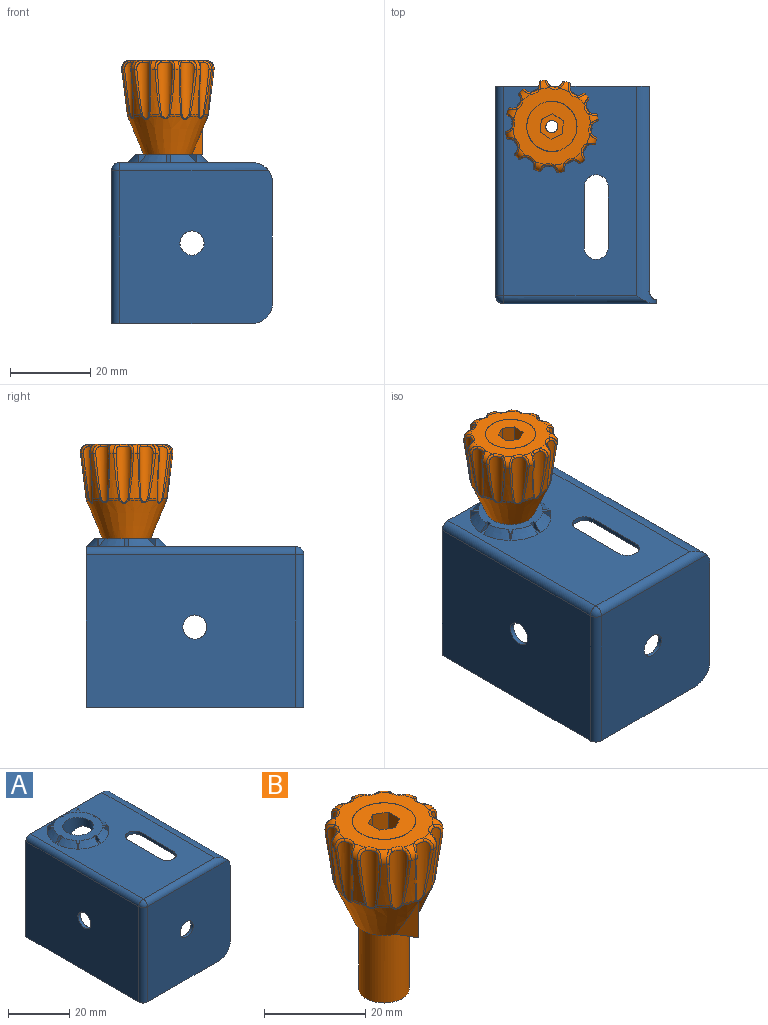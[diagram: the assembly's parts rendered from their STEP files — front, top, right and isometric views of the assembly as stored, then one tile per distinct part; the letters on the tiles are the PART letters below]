
ASSEMBLY  parts=2 mates=1
PART A: 58 faces, bbox 40.1x54.1x42.1 mm
  f0: plane 52x33mm, normal (0,0,1), area 1293.7mm2, adj f5,f6,f12,f13,f14,f15,f17,f18
  f1: plane 51x19.73mm, normal (0,0,-1), area 886.5mm2, adj f5,f6,f9,f12,f13,f14,f15,f16
  f2: plane 54x35mm, normal (0,0,-1), area 96.3mm2, adj f4,f6,f7,f8,f10,f11,f31,f33
  f3: plane 30x1mm, normal (1,0,0), area 30mm2, adj f4,f5,f8,f11
  f4: cylinder r=5mm len=5mm, axis (0,-1,0), area 7.9mm2, adj f2,f3,f8,f11
  f5: cylinder r=5mm len=54mm, axis (0,-1,0), area 189.4mm2, adj f0,f1,f3,f6,f8,f11,f30,f32
  f6: plane 40x38.2mm, normal (0,1,0), area 236.8mm2, adj f0,f1,f2,f5,f7,f9,f10,f35
  f7: plane 52x38mm, normal (-1,0,0), area 1947.7mm2, adj f2,f6,f33,f35,f36
  f8: plane 38x38mm, normal (0,-1,0), area 1409.4mm2, adj f2,f3,f4,f5,f32,f33,f37
  f9: plane 53x17.31mm, normal (0.71,0,-0.71), area 1178.5mm2, adj f1,f6,f10,f11,f16,f30,f31,f36
  f10: plane 51x21.54mm, normal (1,0,0), area 1075.4mm2, adj f2,f6,f9,f31,f36
  f11: plane 36.84x36.84mm, normal (0,1,0), area 1235.1mm2, adj f2,f3,f4,f5,f9,f30,f31,f37
  f12: plane 15x1.16mm, normal (-1,0,0), area 17.3mm2, adj f0,f1,f13,f15
  f13: cylinder r=3mm len=6mm, axis (0,0,1), area 10.9mm2, adj f0,f1,f12,f14
  f14: plane 15x1.16mm, normal (1,0,0), area 17.3mm2, adj f0,f1,f13,f15
  f15: cylinder r=3mm len=6mm, axis (0,0,1), area 10.9mm2, adj f0,f1,f12,f14
  f16: cylinder r=5mm len=12.67mm, axis (0,0,1), area 241.1mm2, adj f1,f9,f29
  f17: plane 2.55x2.01mm, normal (0,-1,0), area 3.1mm2, adj f0,f18,f29,f42
  f18: plane 2x1mm, normal (-1,0,0), area 2mm2, adj f0,f17,f19,f29
  f19: plane 2.55x2.01mm, normal (0,1,0), area 3.1mm2, adj f0,f18,f29,f41
  f20: plane 2.55x2.01mm, normal (1,0,0), area 3.1mm2, adj f0,f21,f29,f40
  f21: plane 2x1mm, normal (0,-1,0), area 2mm2, adj f0,f20,f22,f29
  f22: plane 2.55x2.01mm, normal (-1,0,0), area 3.1mm2, adj f0,f21,f29,f44
  f23: plane 2.55x2.01mm, normal (0,1,0), area 3.1mm2, adj f0,f24,f29,f39
  f24: plane 2x1mm, normal (1,0,0), area 2mm2, adj f0,f23,f25,f29
  f25: plane 2.55x2.01mm, normal (0,-1,0), area 3.1mm2, adj f0,f24,f29,f38
  f26: plane 2.55x2.01mm, normal (-1,0,0), area 3.1mm2, adj f0,f27,f29,f45
  f27: plane 2x1mm, normal (0,1,0), area 2mm2, adj f0,f26,f28,f29
  f28: plane 2.55x2.01mm, normal (1,0,0), area 3.1mm2, adj f0,f27,f29,f43
  f29: plane 15.97x15.97mm, normal (0,0,1), area 125.2mm2, adj f16,f17,f18,f19,f20,f21,f22,f23
  f30: cylinder r=2mm len=23.18mm, axis (1,0,0), area 66.3mm2, adj f1,f5,f9,f11
  f31: cylinder r=2mm len=23.54mm, axis (0,0,1), area 69.9mm2, adj f2,f9,f10,f11
  f32: cylinder r=2mm len=37mm, axis (-1,0,0), area 110.7mm2, adj f0,f5,f8,f34
  f33: cylinder r=2mm len=38mm, axis (0,0,-1), area 119.4mm2, adj f2,f7,f8,f34
  f34: sphere r=2mm, area 6.3mm2, adj f32,f33,f35
  f35: cylinder r=2mm len=52mm, axis (0,-1,0), area 163.4mm2, adj f0,f6,f7,f34
  f36: cylinder r=3mm len=6mm, axis (-1,0,0), area 27.7mm2, adj f7,f9,f10
  f37: cylinder r=3mm len=6mm, axis (0,-1,0), area 18.8mm2, adj f8,f11
  f38: cone r=10mm half-angle=45deg, axis (0,0,-1), area 17.5mm2, adj f0,f25,f29,f46
  f39: cone r=8mm half-angle=45deg, axis (0,0,-1), area 17.8mm2, adj f0,f23,f29,f49
  f40: cone r=10mm half-angle=45deg, axis (0,0,-1), area 17.8mm2, adj f0,f20,f29,f55
  f41: cone r=8mm half-angle=45deg, axis (0,0,-1), area 17.8mm2, adj f0,f19,f29,f56
  f42: cone r=8mm half-angle=45deg, axis (0,0,-1), area 17.5mm2, adj f0,f17,f29,f52
  f43: cone r=8mm half-angle=45deg, axis (0,0,-1), area 17.8mm2, adj f0,f28,f29,f53
  f44: cone r=8mm half-angle=45deg, axis (0,0,-1), area 17.5mm2, adj f0,f22,f29,f50
  f45: cone r=8mm half-angle=45deg, axis (0,0,-1), area 17.5mm2, adj f0,f26,f29,f48
  f46: plane 2.06x1.82mm, normal (0.85,-0.53,0), area 2.1mm2, adj f29,f38,f47
  f47: cylinder r=10mm len=2mm, axis (0,0,-1), area 0.3mm2, adj f0,f29,f46,f48
  f48: plane 2.06x1.82mm, normal (-0.53,0.85,0), area 2.1mm2, adj f29,f45,f47
  f49: plane 2.06x1.82mm, normal (0.85,0.53,0), area 2.1mm2, adj f29,f39,f51
  f50: plane 2.06x1.82mm, normal (-0.53,-0.85,0), area 2.1mm2, adj f29,f44,f51
  f51: cylinder r=10mm len=2mm, axis (0,0,-1), area 0.3mm2, adj f0,f29,f49,f50
  f52: plane 2.06x1.82mm, normal (-0.85,-0.53,0), area 2.1mm2, adj f29,f42,f54
  f53: plane 2.06x1.82mm, normal (0.53,0.85,0), area 2.1mm2, adj f29,f43,f54
  f54: cylinder r=10mm len=2mm, axis (0,0,-1), area 0.3mm2, adj f0,f29,f52,f53
  f55: plane 2.06x2mm, normal (0.53,-0.85,0), area 2.5mm2, adj f0,f29,f40,f57
  f56: plane 2.06x2mm, normal (-0.85,0.53,0), area 2.5mm2, adj f0,f29,f41,f57
  f57: cylinder r=0.02mm len=2mm, axis (0,0,-1), area 0.1mm2, adj f0,f29,f55,f56
PART B: 171 faces, bbox 23.8x23.8x41.5 mm
  f0: cylinder r=1.5mm len=5.5mm, axis (0,0,1), area 51.8mm2, adj f40,f159
  f1: plane 12.45x12.45mm, normal (0,0,1), area 95.5mm2, adj f152,f153,f154,f155,f156,f157,f158
  f2: torus R=9.64mm, axis (0,0,-1), area 4.8mm2, adj f14,f43,f56,f91
  f3: torus R=9.64mm, axis (0,0,-1), area 4.8mm2, adj f16,f43,f138,f145
  f4: torus R=9.64mm, axis (0,0,-1), area 4.8mm2, adj f17,f43,f64,f99
  f5: torus R=9.64mm, axis (0,0,-1), area 4.8mm2, adj f19,f43,f59,f72
  f6: torus R=9.64mm, axis (0,0,-1), area 4.8mm2, adj f21,f43,f67,f83
  f7: torus R=9.64mm, axis (0,0,-1), area 4.8mm2, adj f22,f43,f108,f146
  f8: torus R=9.64mm, axis (0,0,-1), area 4.8mm2, adj f15,f43,f88,f137
  f9: torus R=9.64mm, axis (0,0,-1), area 4.8mm2, adj f23,f43,f96,f124
  f10: torus R=9.64mm, axis (0,0,-1), area 4.8mm2, adj f24,f43,f104,f131
  f11: torus R=9.64mm, axis (0,0,-1), area 4.8mm2, adj f20,f43,f80,f112
  f12: torus R=9.64mm, axis (0,0,-1), area 4.8mm2, adj f18,f43,f76,f120
  f13: torus R=9.64mm, axis (0,0,-1), area 4.8mm2, adj f25,f43,f115,f128
  f14: cone r=10.11mm half-angle=7.8deg, axis (0,0,1), area 18.4mm2, adj f2,f30,f58,f93
  f15: cone r=10.11mm half-angle=7.8deg, axis (0,0,1), area 18.4mm2, adj f8,f28,f90,f139
  f16: cone r=10.11mm half-angle=7.8deg, axis (0,0,1), area 18.4mm2, adj f3,f27,f140,f147
  f17: cone r=10.11mm half-angle=7.8deg, axis (0,0,1), area 18.4mm2, adj f4,f32,f66,f101
  f18: cone r=10.11mm half-angle=7.8deg, axis (0,0,1), area 18.4mm2, adj f12,f31,f78,f121
  f19: cone r=10.11mm half-angle=7.8deg, axis (0,0,1), area 18.4mm2, adj f5,f26,f61,f73
  f20: cone r=10.11mm half-angle=7.8deg, axis (0,0,1), area 18.4mm2, adj f11,f33,f82,f114
  f21: cone r=10.11mm half-angle=7.8deg, axis (0,0,1), area 18.4mm2, adj f6,f29,f69,f85
  f22: cone r=10.11mm half-angle=7.8deg, axis (0,0,1), area 18.4mm2, adj f7,f34,f110,f148
  f23: cone r=10.11mm half-angle=7.8deg, axis (0,0,1), area 18.4mm2, adj f9,f37,f98,f126
  f24: cone r=10.11mm half-angle=7.8deg, axis (0,0,1), area 18.4mm2, adj f10,f35,f105,f133
  f25: cone r=10.11mm half-angle=7.8deg, axis (0,0,1), area 18.4mm2, adj f13,f36,f117,f130
  f26: torus R=8.13mm, axis (0,0,-1), area 1.5mm2, adj f19,f38,f63,f75
  f27: torus R=8.13mm, axis (0,0,-1), area 1.5mm2, adj f16,f38,f142,f149
  f28: torus R=8.13mm, axis (0,0,-1), area 1.5mm2, adj f15,f38,f92,f141
  f29: torus R=8.13mm, axis (0,0,-1), area 1.5mm2, adj f21,f38,f71,f87
  f30: torus R=8.13mm, axis (0,0,-1), area 1.5mm2, adj f14,f38,f60,f95
  f31: torus R=8.13mm, axis (0,0,-1), area 1.5mm2, adj f18,f38,f79,f123
  f32: torus R=8.13mm, axis (0,0,-1), area 1.5mm2, adj f17,f38,f68,f103
  f33: torus R=8.13mm, axis (0,0,-1), area 1.5mm2, adj f20,f38,f84,f116
  f34: torus R=8.13mm, axis (0,0,-1), area 1.5mm2, adj f22,f38,f111,f150
  f35: torus R=8.13mm, axis (0,0,-1), area 1.5mm2, adj f24,f38,f107,f135
  f36: torus R=8.13mm, axis (0,0,-1), area 1.5mm2, adj f25,f38,f119,f132
  f37: torus R=8.13mm, axis (0,0,-1), area 1.5mm2, adj f23,f38,f100,f127
  f38: cone r=6mm half-angle=22.6deg, axis (0,0,1), area 482.2mm2, adj f26,f27,f28,f29,f30,f31,f32,f33
  f39: cylinder r=5mm len=17mm, axis (0,0,1), area 534.1mm2, adj f40,f41
  f40: plane 10x10mm, normal (0,0,-1), area 71.5mm2, adj f0,f39
  f41: plane 15.64x12mm, normal (0,0,-1), area 42.8mm2, adj f38,f39,f169,f170
  f42: torus R=6.25mm, axis (0,0,-1), area 1.2mm2, adj f43,f152
  f43: plane 19.12x19.1mm, normal (0,0,1), area 160.1mm2, adj f2,f3,f4,f5,f6,f7,f8,f9
  f44: cylinder r=2mm len=13.83mm, axis (0,0,1), area 47.1mm2, adj f128,f129,f130,f131,f132,f133,f134,f135
  f45: cylinder r=2mm len=13.94mm, axis (0,0,1), area 48.6mm2, adj f120,f121,f122,f123,f124,f125,f126,f127
  f46: cylinder r=2mm len=13.94mm, axis (0,0,1), area 48.6mm2, adj f112,f113,f114,f115,f116,f117,f118,f119
  f47: cylinder r=2mm len=13.94mm, axis (0,0,1), area 48.6mm2, adj f104,f105,f106,f107,f108,f109,f110,f111
  f48: cylinder r=2mm len=13.83mm, axis (0,0,1), area 47.1mm2, adj f96,f97,f98,f99,f100,f101,f102,f103
  f49: cylinder r=2mm len=13.83mm, axis (0,0,1), area 47.1mm2, adj f88,f89,f90,f91,f92,f93,f94,f95
  f50: cylinder r=2mm len=13.83mm, axis (0,0,1), area 47.1mm2, adj f144,f145,f146,f147,f148,f149,f150,f151
  f51: cylinder r=2mm len=13.83mm, axis (0,0,1), area 47.1mm2, adj f80,f81,f82,f83,f84,f85,f86,f87
  f52: cylinder r=2mm len=13.83mm, axis (0,0,1), area 47.1mm2, adj f72,f73,f74,f75,f76,f77,f78,f79
  f53: cylinder r=2mm len=13.94mm, axis (0,0,1), area 48.6mm2, adj f64,f65,f66,f67,f68,f69,f70,f71
  f54: cylinder r=2mm len=13.94mm, axis (0,0,1), area 48.6mm2, adj f136,f137,f138,f139,f140,f141,f142,f143
  f55: cylinder r=2mm len=13.94mm, axis (0,0,1), area 48.6mm2, adj f56,f57,f58,f59,f60,f61,f62,f63
  f56: bspline ~2.74x2.27mm, area 2.2mm2, adj f2,f55,f57,f58
  f57: torus R=2.5mm, axis (0,0,1), area 1.9mm2, adj f43,f55,f56,f59
  f58: bspline ~15.1x2.39mm, area 6.2mm2, adj f14,f55,f56,f60
  f59: bspline ~2.64x2.44mm, area 2.2mm2, adj f5,f55,f57,f61
  f60: bspline ~0.87x0.6mm, area 0.2mm2, adj f30,f55,f58,f62
  f61: bspline ~12.62x2.15mm, area 6.2mm2, adj f19,f55,f59,f63
  f62: bspline ~2.6x1.52mm, area 0.7mm2, adj f38,f55,f60,f63
  f63: bspline ~0.85x0.38mm, area 0.2mm2, adj f26,f55,f61,f62
  f64: bspline ~2.74x2.12mm, area 2.2mm2, adj f4,f53,f65,f66
  f65: torus R=2.5mm, axis (0,0,1), area 1.9mm2, adj f43,f53,f64,f67
  f66: bspline ~15.1x2mm, area 6.2mm2, adj f17,f53,f64,f68
  f67: bspline ~2.44x2.22mm, area 2.2mm2, adj f6,f53,f65,f69
  f68: bspline ~0.87x0.59mm, area 0.2mm2, adj f32,f53,f66,f70
  f69: bspline ~12.62x1.66mm, area 6.2mm2, adj f21,f53,f67,f71
  f70: bspline ~3x1.52mm, area 0.7mm2, adj f38,f53,f68,f71
  f71: bspline ~0.85x0.49mm, area 0.2mm2, adj f29,f53,f69,f70
  f72: bspline ~2.74x2.09mm, area 2.2mm2, adj f5,f52,f73,f74
  f73: bspline ~14.64x1.94mm, area 6mm2, adj f19,f52,f72,f75
  f74: torus R=2.5mm, axis (0,0,1), area 1.8mm2, adj f43,f52,f72,f76
  f75: bspline ~0.86x0.58mm, area 0.2mm2, adj f26,f52,f73,f77
  f76: bspline ~2.75x2.2mm, area 2.2mm2, adj f12,f52,f74,f78
  f77: bspline ~2.82x1.35mm, area 0.6mm2, adj f38,f52,f75,f79
  f78: bspline ~15.26x2mm, area 6mm2, adj f18,f52,f76,f79
  f79: bspline ~0.84x0.49mm, area 0.2mm2, adj f31,f52,f77,f78
  f80: bspline ~2.75x2.51mm, area 2.2mm2, adj f11,f51,f81,f82
  f81: torus R=2.5mm, axis (0,0,1), area 1.8mm2, adj f43,f51,f80,f83
  f82: bspline ~15.26x2.46mm, area 6mm2, adj f20,f51,f80,f84
  f83: bspline ~2.74x2.47mm, area 2.2mm2, adj f6,f51,f81,f85
  f84: bspline ~0.84x0.5mm, area 0.2mm2, adj f33,f51,f82,f86
  f85: bspline ~14.64x2.41mm, area 6mm2, adj f21,f51,f83,f87
  f86: bspline ~2.44x1.41mm, area 0.6mm2, adj f38,f51,f84,f87
  f87: bspline ~0.86x0.45mm, area 0.2mm2, adj f29,f51,f85,f86
  f88: bspline ~2.74x2.47mm, area 2.2mm2, adj f8,f49,f89,f90
  f89: torus R=2.5mm, axis (0,0,1), area 1.8mm2, adj f43,f49,f88,f91
  f90: bspline ~14.64x2.41mm, area 6mm2, adj f15,f49,f88,f92
  f91: bspline ~2.75x2.51mm, area 2.2mm2, adj f2,f49,f89,f93
  f92: bspline ~0.86x0.45mm, area 0.2mm2, adj f28,f49,f90,f94
  f93: bspline ~15.26x2.46mm, area 6mm2, adj f14,f49,f91,f95
  f94: bspline ~2.44x1.41mm, area 0.6mm2, adj f38,f49,f92,f95
  f95: bspline ~0.84x0.5mm, area 0.2mm2, adj f30,f49,f93,f94
  f96: bspline ~2.74x2.28mm, area 2.2mm2, adj f9,f48,f97,f98
  f97: torus R=2.5mm, axis (0,0,1), area 1.8mm2, adj f43,f48,f96,f99
  f98: bspline ~14.64x2.34mm, area 6mm2, adj f23,f48,f96,f100
  f99: bspline ~2.75x2.67mm, area 2.2mm2, adj f4,f48,f97,f101
  f100: bspline ~0.86x0.6mm, area 0.2mm2, adj f37,f48,f98,f102
  f101: bspline ~15.26x2.51mm, area 6mm2, adj f17,f48,f99,f103
  f102: bspline ~2.44x1.41mm, area 0.6mm2, adj f38,f48,f100,f103
  f103: bspline ~0.84x0.37mm, area 0.2mm2, adj f32,f48,f101,f102
  f104: bspline ~2.74x2.48mm, area 2.2mm2, adj f10,f47,f105,f106
  f105: bspline ~15.1x2.47mm, area 6.2mm2, adj f24,f47,f104,f107
  f106: torus R=2.5mm, axis (0,0,1), area 1.9mm2, adj f43,f47,f104,f108
  f107: bspline ~0.87x0.46mm, area 0.2mm2, adj f35,f47,f105,f109
  f108: bspline ~2.46x2.44mm, area 2.2mm2, adj f7,f47,f106,f110
  f109: bspline ~2.6x1.52mm, area 0.7mm2, adj f38,f47,f107,f111
  f110: bspline ~12.62x2.16mm, area 6.2mm2, adj f22,f47,f108,f111
  f111: bspline ~0.85x0.51mm, area 0.2mm2, adj f34,f47,f109,f110
  f112: bspline ~2.74x2.27mm, area 2.2mm2, adj f11,f46,f113,f114
  f113: torus R=2.5mm, axis (0,0,1), area 1.9mm2, adj f43,f46,f112,f115
  f114: bspline ~15.1x2.39mm, area 6.2mm2, adj f20,f46,f112,f116
  f115: bspline ~2.64x2.44mm, area 2.2mm2, adj f13,f46,f113,f117
  f116: bspline ~0.87x0.6mm, area 0.2mm2, adj f33,f46,f114,f118
  f117: bspline ~12.62x2.15mm, area 6.2mm2, adj f25,f46,f115,f119
  f118: bspline ~2.32x1.52mm, area 0.7mm2, adj f38,f46,f116,f119
  f119: bspline ~0.85x0.38mm, area 0.2mm2, adj f36,f46,f117,f118
  f120: bspline ~2.74x2.48mm, area 2.2mm2, adj f12,f45,f121,f122
  f121: bspline ~15.1x2.47mm, area 6.2mm2, adj f18,f45,f120,f123
  f122: torus R=2.5mm, axis (0,0,1), area 1.9mm2, adj f43,f45,f120,f124
  f123: bspline ~0.87x0.46mm, area 0.2mm2, adj f31,f45,f121,f125
  f124: bspline ~2.46x2.44mm, area 2.2mm2, adj f9,f45,f122,f126
  f125: bspline ~2.6x1.52mm, area 0.7mm2, adj f38,f45,f123,f127
  f126: bspline ~12.62x2.16mm, area 6.2mm2, adj f23,f45,f124,f127
  f127: bspline ~0.85x0.51mm, area 0.2mm2, adj f37,f45,f125,f126
  f128: bspline ~2.74x2.09mm, area 2.2mm2, adj f13,f44,f129,f130
  f129: torus R=2.5mm, axis (0,0,1), area 1.8mm2, adj f43,f44,f128,f131
  f130: bspline ~14.64x1.94mm, area 6mm2, adj f25,f44,f128,f132
  f131: bspline ~2.75x2.2mm, area 2.2mm2, adj f10,f44,f129,f133
  f132: bspline ~0.86x0.58mm, area 0.2mm2, adj f36,f44,f130,f134
  f133: bspline ~15.26x2mm, area 6mm2, adj f24,f44,f131,f135
  f134: bspline ~2.82x1.35mm, area 0.6mm2, adj f38,f44,f132,f135
  f135: bspline ~0.84x0.49mm, area 0.2mm2, adj f35,f44,f133,f134
  f136: torus R=2.5mm, axis (0,0,1), area 1.9mm2, adj f43,f54,f137,f138
  f137: bspline ~2.44x2.22mm, area 2.2mm2, adj f8,f54,f136,f139
  f138: bspline ~2.74x2.12mm, area 2.2mm2, adj f3,f54,f136,f140
  f139: bspline ~15.1x2mm, area 6.2mm2, adj f15,f54,f137,f141
  f140: bspline ~15.1x2mm, area 6.2mm2, adj f16,f54,f138,f142
  f141: bspline ~0.85x0.49mm, area 0.2mm2, adj f28,f54,f139,f143
  f142: bspline ~0.87x0.59mm, area 0.2mm2, adj f27,f54,f140,f143
  f143: bspline ~3x1.52mm, area 0.7mm2, adj f38,f54,f141,f142
  f144: torus R=2.5mm, axis (0,0,1), area 1.8mm2, adj f43,f50,f145,f146
  f145: bspline ~2.75x2.67mm, area 2.2mm2, adj f3,f50,f144,f147
  f146: bspline ~2.74x2.28mm, area 2.2mm2, adj f7,f50,f144,f148
  f147: bspline ~15.26x2.51mm, area 6mm2, adj f16,f50,f145,f149
  f148: bspline ~14.64x2.34mm, area 6mm2, adj f22,f50,f146,f150
  f149: bspline ~0.84x0.37mm, area 0.2mm2, adj f27,f50,f147,f151
  f150: bspline ~0.86x0.6mm, area 0.2mm2, adj f34,f50,f148,f151
  f151: bspline ~2.44x1.41mm, area 0.6mm2, adj f38,f50,f149,f150
  f152: cylinder r=6.22mm len=12.45mm, axis (0,0,1), area 0mm2, adj f1,f42
  f153: plane 22.4x2.75mm, normal (-0.5,-0.87,0), area 71.1mm2, adj f1,f154,f158,f168
  f154: plane 22.4x3.18mm, normal (-1,0,0), area 71.1mm2, adj f1,f153,f155,f168
  f155: plane 22.4x2.75mm, normal (-0.5,0.87,0), area 71.1mm2, adj f1,f154,f156,f168
  f156: plane 22.4x2.75mm, normal (0.5,0.87,0), area 71.1mm2, adj f1,f155,f157,f168
  f157: plane 22.4x3.18mm, normal (1,0,0), area 71.1mm2, adj f1,f156,f158,f168
  f158: plane 22.4x2.75mm, normal (0.5,-0.87,0), area 71.1mm2, adj f1,f153,f157,f168
  f159: plane 6.35x5.5mm, normal (0,0,1), area 19.1mm2, adj f0,f160,f161,f162,f163,f164,f165
  f160: plane 11.5x2.75mm, normal (0.5,-0.87,0), area 36.5mm2, adj f159,f161,f165,f166
  f161: plane 11.5x3.18mm, normal (1,0,0), area 36.5mm2, adj f159,f160,f162,f166
  f162: plane 11.5x2.75mm, normal (0.5,0.87,0), area 36.5mm2, adj f159,f161,f163,f166
  f163: plane 11.5x2.75mm, normal (-0.5,0.87,0), area 36.5mm2, adj f159,f162,f164,f166
  f164: plane 11.5x3.18mm, normal (-1,0,0), area 36.5mm2, adj f159,f163,f165,f166
  f165: plane 11.5x2.75mm, normal (-0.5,-0.87,0), area 36.5mm2, adj f159,f160,f164,f166
  f166: plane 8x8mm, normal (0,0,1), area 24.1mm2, adj f160,f161,f162,f163,f164,f165,f167
  f167: cylinder r=4mm len=8mm, axis (0,0,-1), area 24.3mm2, adj f166,f168
  f168: plane 8x8mm, normal (0,0,-1), area 24.1mm2, adj f153,f154,f155,f156,f157,f158,f167
  f169: plane 8.72x4.12mm, normal (-0.87,-0.5,0), area 19.5mm2, adj f38,f41,f170
  f170: plane 8.72x4.12mm, normal (0.87,-0.5,0), area 19.5mm2, adj f38,f41,f169
PLACE A t=(9.24,-27.73,-7.84)mm fixed
PLACE B rot(axis=(0,0,1),116.2deg) t=(3.24,16.27,14.16)mm
MATE revolute B.f2 <-> A.f16  axis (0,0,1) through (3.24,16.27,14.16)mm
